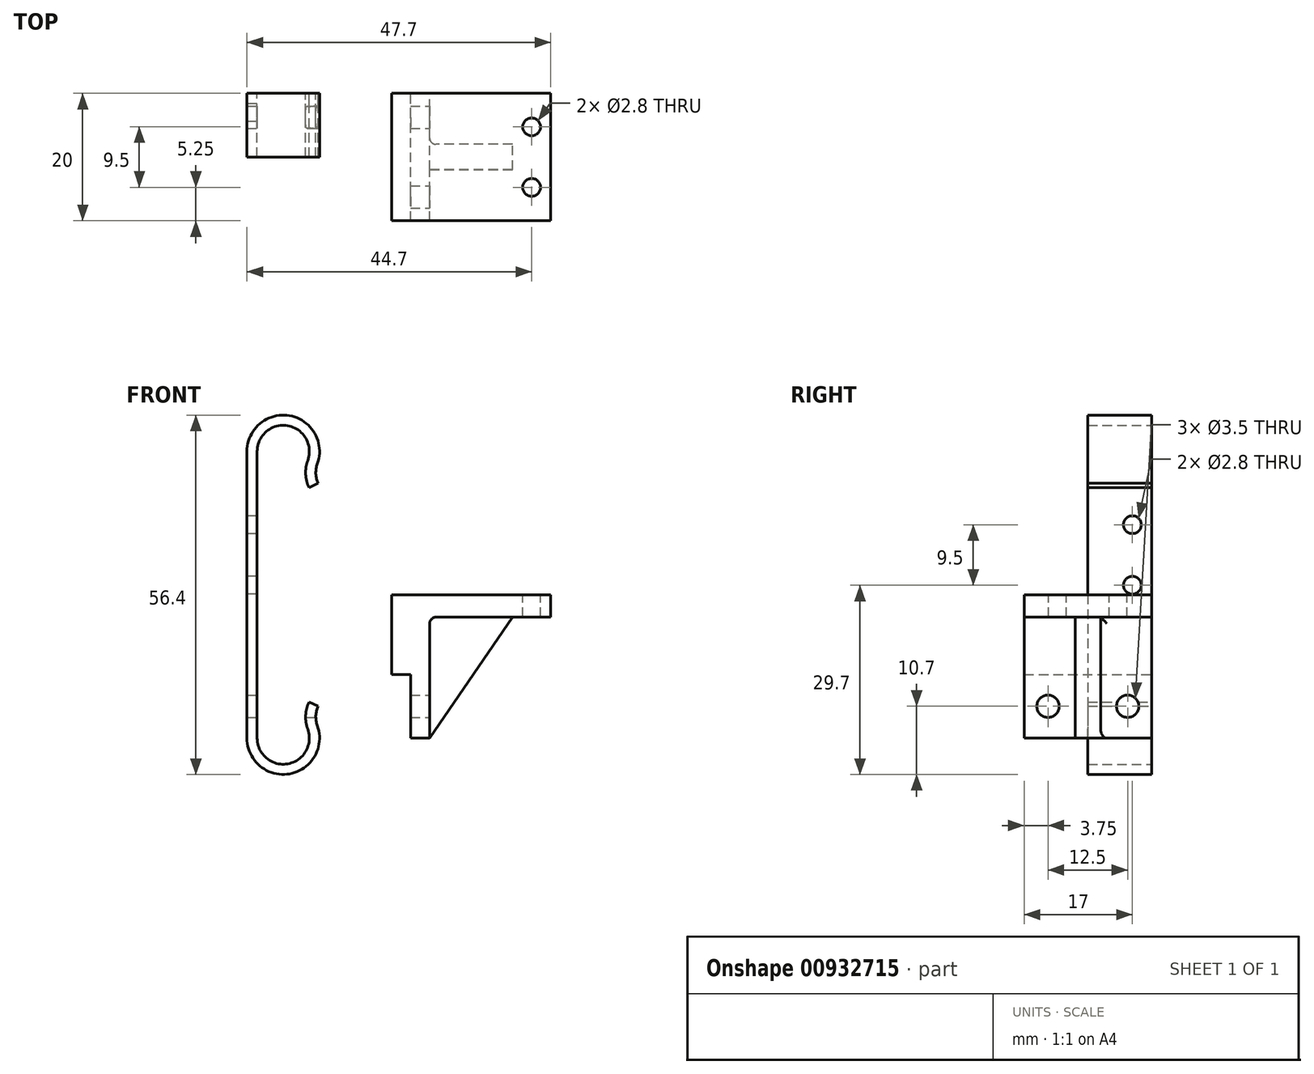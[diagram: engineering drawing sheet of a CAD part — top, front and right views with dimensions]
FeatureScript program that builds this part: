
annotation { "Feature Type Name" : "Feature", "Feature Type Description" : "" }
export const myFeature = defineFeature(function(context is Context, id is Id, definition is map)
    precondition{}
    {
        {
            var Q0;
            Q0=qCreatedBy(makeId("Front.planeOp"),FACE);
            var sketch = newSketch(context, id + "F0", { "sketchPlane" : qUnion([Q0])});
            skLineSegment(sketch, "E0", {"start": v(-25.7, 45) * mm, "end": v(-25.7, 0) * mm});
            skLineSegment(sketch, "E1", {"start": v(-24.1, 45) * mm, "end": v(-24.1, 0) * mm});
            skArc(sketch, "E2", {"start": v(-14.64, 43.05) * mm, "mid": v(-19.01, 50.61) * mm, "end": v(-25.7, 45) * mm});
            skArc(sketch, "E3", {"start": v(-16.15, 43.6) * mm, "mid": v(-19.29, 49.04) * mm, "end": v(-24.1, 45) * mm});
            skArc(sketch, "E4", {"start": v(-24.1, 0) * mm, "mid": v(-19.29, -4.04) * mm, "end": v(-16.15, 1.4) * mm});
            skArc(sketch, "E5", {"start": v(-25.7, 0) * mm, "mid": v(-19.01, -5.61) * mm, "end": v(-14.64, 1.95) * mm});
            skArc(sketch, "E6", {"start": v(-16.15, 43.6) * mm, "mid": v(-16.48, 41.44) * mm, "end": v(-15.96, 39.32) * mm});
            skArc(sketch, "E7", {"start": v(-15.96, 5.68) * mm, "mid": v(-16.48, 3.56) * mm, "end": v(-16.15, 1.4) * mm});
            skLineSegment(sketch, "E8", {"start": v(-20, 0) * mm, "end": v(-16.15, 1.4) * mm, "construction": true});
            skLineSegment(sketch, "E9", {"start": v(-20, 0) * mm, "end": v(-24.1, 0) * mm, "construction": true});
            skLineSegment(sketch, "E10", {"start": v(-10.88, 3.32) * mm, "end": v(-15.96, 5.68) * mm, "construction": true});
            skArc(sketch, "E11", {"start": v(-14.51, 5) * mm, "mid": v(-14.88, 3.5) * mm, "end": v(-14.64, 1.95) * mm});
            skArc(sketch, "E12", {"start": v(-14.64, 43.05) * mm, "mid": v(-14.88, 41.5) * mm, "end": v(-14.51, 40) * mm});
            skLineSegment(sketch, "E13", {"start": v(-14.51, 40) * mm, "end": v(-15.96, 39.32) * mm});
            skLineSegment(sketch, "E14", {"start": v(-20, 45) * mm, "end": v(-16.15, 43.6) * mm, "construction": true});
            skLineSegment(sketch, "E15", {"start": v(-15.96, 5.68) * mm, "end": v(-14.51, 5) * mm});
            skLineSegment(sketch, "E16", {"start": v(-20, 0) * mm, "end": v(0, 0) * mm, "construction": true});
            skSolve(sketch);
        }
        {
            var Q0;
            Q0=makeQuery(id+"F0.imprint","IMPRINT",FACE,{"disambiguationData":[TD([[makeQuery(id+"F0.imprint","IMPRINT",EDGE,{"derivedFrom":sQuery(id+"F0.wireOp",EDGE,"E0")}),1.0]])]});
            extrude(context, id + "F1", {"entities" : qUnion([Q0]), "depth" : 10 * mm, "offsetDistance" : 25 * mm});
        }
        {
            var Q0;
            Q0=makeQuery(id+"F1.opExtrude","SWEPT_FACE",FACE,{"disambiguationData":[OSD([sQuery(id+"F0.wireOp",EDGE,"E0")])]});
            var sketch = newSketch(context, id + "F2", { "sketchPlane" : qUnion([Q0])});
            skCircle(sketch, "E17", {"center": v(3, 33.5) * mm, "radius": 1.4 * mm});
            skCircle(sketch, "E18", {"center": v(3, 24) * mm, "radius": 1.4 * mm});
            skLineSegment(sketch, "E19", {"start": v(3, 33.5) * mm, "end": v(3, 24) * mm, "construction": true});
            skSolve(sketch);
        }
        {
            var Q0;
            Q0 = qSketchRegion(id + "F2", true);
            extrude(context, id + "F3", {"entities" : qUnion([Q0]), "operationType" : NewBodyOperationType.REMOVE, "endBound" : BoundingType.THROUGH_ALL, "oppositeDirection" : true, "depth" : 25 * mm, "offsetDistance" : 25 * mm});
        }
        {
            var Q0;
            Q0=qCreatedBy(makeId("Front.planeOp"),FACE);
            var sketch = newSketch(context, id + "F4", { "sketchPlane" : qUnion([Q0])});
            skLineSegment(sketch, "E20", {"start": v(0, 0) * mm, "end": v(0, 10) * mm});
            skLineSegment(sketch, "E21", {"start": v(0, 10) * mm, "end": v(-3, 10) * mm});
            skLineSegment(sketch, "E22", {"start": v(-3, 10) * mm, "end": v(-3, 22.5) * mm});
            skLineSegment(sketch, "E23", {"start": v(-3, 22.5) * mm, "end": v(22, 22.5) * mm});
            skLineSegment(sketch, "E24", {"start": v(22, 22.5) * mm, "end": v(22, 19) * mm});
            skLineSegment(sketch, "E25", {"start": v(22, 19) * mm, "end": v(3, 19) * mm});
            skLineSegment(sketch, "E26", {"start": v(3, 19) * mm, "end": v(3, 0) * mm});
            skLineSegment(sketch, "E27", {"start": v(3, 0) * mm, "end": v(0, 0) * mm});
            skSolve(sketch);
        }
        {
            var Q0;
            Q0=makeQuery(id+"F4.imprint","IMPRINT",FACE,{"disambiguationData":[TD([[makeQuery(id+"F4.imprint","IMPRINT",EDGE,{"derivedFrom":sQuery(id+"F4.wireOp",EDGE,"E20")}),-1.0]])]});
            extrude(context, id + "F5", {"entities" : qUnion([Q0]), "depth" : 20 * mm, "offsetDistance" : 25 * mm});
        }
        {
            var Q0;
            Q0=makeQuery(id+"F5.opExtrude","SWEPT_FACE",FACE,{"disambiguationData":[OSD([sQuery(id+"F4.wireOp",EDGE,"E23")])]});
            var sketch = newSketch(context, id + "F6", { "sketchPlane" : qUnion([Q0])});
            skCircle(sketch, "E28", {"center": v(19, -5.25) * mm, "radius": 1.4 * mm});
            skCircle(sketch, "E29", {"center": v(19, -14.75) * mm, "radius": 1.4 * mm});
            skLineSegment(sketch, "E30", {"start": v(19, -5.25) * mm, "end": v(19, -14.75) * mm, "construction": true});
            skLineSegment(sketch, "E31", {"start": v(19, -10) * mm, "end": v(22, -10) * mm, "construction": true});
            skSolve(sketch);
        }
        {
            var Q0;
            Q0 = qSketchRegion(id + "F6", true);
            extrude(context, id + "F7", {"entities" : qUnion([Q0]), "operationType" : NewBodyOperationType.REMOVE, "endBound" : BoundingType.THROUGH_ALL, "oppositeDirection" : true, "depth" : 25 * mm, "offsetDistance" : 25 * mm});
        }
        {
            var Q0;
            Q0=makeQuery(id+"F5.opExtrude","SWEPT_EDGE",EDGE,{"disambiguationData":[OSD([sQuery(id+"F4.wireOp",EDGE,"E24"),sQuery(id+"F4.wireOp",EDGE,"E25")])]});
            cPoint(context, id + "F8", {"entities" : qUnion([Q0]), "parameter" : 0.5});
        }
        {
            var Q0;
            Q0=makeQuery(id+"F5.opExtrude","CAP_FACE",FACE,{"disambiguationData":[OSD([sQuery(id+"F4.wireOp",EDGE,"E20"),sQuery(id+"F4.wireOp",EDGE,"E21"),sQuery(id+"F4.wireOp",EDGE,"E22"),sQuery(id+"F4.wireOp",EDGE,"E23"),sQuery(id+"F4.wireOp",EDGE,"E24"),sQuery(id+"F4.wireOp",EDGE,"E25"),sQuery(id+"F4.wireOp",EDGE,"E26"),sQuery(id+"F4.wireOp",EDGE,"E27")])],"isStart":false});
            var Q1;
            Q1 = qCreatedBy(id + "F8" ,VERTEX);
            cPlane(context, id + "F9", {"entities" : qUnion([Q0, Q1]), "cplaneType" : CPlaneType.PLANE_POINT, "offset" : 25 * mm, "width" : 150 * mm, "height" : 150 * mm});
        }
        {
            var Q0;
            Q0=qCreatedBy(id+"F9.planeOp",FACE);
            var sketch = newSketch(context, id + "F10", { "sketchPlane" : qUnion([Q0])});
            skLineSegment(sketch, "E32", {"start": v(3, 0) * mm, "end": v(16, 19) * mm});
            skLineSegment(sketch, "E33", {"start": v(16, 19) * mm, "end": v(3, 19) * mm});
            skLineSegment(sketch, "E34", {"start": v(3, 19) * mm, "end": v(3, 0) * mm});
            skSolve(sketch);
        }
        {
            var Q0;
            Q0=makeQuery(id+"F10.imprint","IMPRINT",FACE,{"disambiguationData":[TD([[makeQuery(id+"F10.imprint","IMPRINT",EDGE,{"derivedFrom":sQuery(id+"F10.wireOp",EDGE,"E32")}),1.0]])]});
            extrude(context, id + "F11", {"entities" : qUnion([Q0]), "operationType" : NewBodyOperationType.ADD, "endBound" : BoundingType.SYMMETRIC, "depth" : 4 * mm, "offsetDistance" : 25 * mm});
        }
        {
            var Q0;
            Q0=makeQuery(id+"F11.opExtrude","CAP_EDGE",EDGE,{"disambiguationData":[OSD([sQuery(id+"F10.wireOp",EDGE,"E33")])],"isStart":false});
            var Q1;
            Q1=makeQuery(id+"F11.opExtrude","CAP_EDGE",EDGE,{"disambiguationData":[OSD([sQuery(id+"F10.wireOp",EDGE,"E34")])],"isStart":false});
            var Q2;
            {var subQ0=sQuery(id+"F4.wireOp",EDGE,"E26");var subQ1=sQuery(id+"F4.wireOp",EDGE,"E25");Q2=makeQuery(id+"F11.boolean.opBoolean","SPLIT",EDGE,{"disambiguationData":[TD([makeQuery(id+"F11.opExtrude","CAP_FACE",FACE,{"disambiguationData":[OSD([sQuery(id+"F10.wireOp",EDGE,"E32"),sQuery(id+"F10.wireOp",EDGE,"E33"),sQuery(id+"F10.wireOp",EDGE,"E34")])],"isStart":false})])],"derivedFrom":makeQuery(id+"F5.opExtrude","SWEPT_EDGE",EDGE,{"disambiguationData":[OSD([subQ1,subQ0])]})});}
            var Q3;
            {var subQ0=sQuery(id+"F4.wireOp",EDGE,"E26");var subQ1=sQuery(id+"F4.wireOp",EDGE,"E25");Q3=makeQuery(id+"F11.boolean.opBoolean","SPLIT",EDGE,{"disambiguationData":[TD([makeQuery(id+"F11.opExtrude","CAP_FACE",FACE,{"disambiguationData":[OSD([sQuery(id+"F10.wireOp",EDGE,"E32"),sQuery(id+"F10.wireOp",EDGE,"E33"),sQuery(id+"F10.wireOp",EDGE,"E34")])],"isStart":true})])],"derivedFrom":makeQuery(id+"F5.opExtrude","SWEPT_EDGE",EDGE,{"disambiguationData":[OSD([subQ1,subQ0])]})});}
            var Q4;
            Q4=makeQuery(id+"F11.opExtrude","CAP_EDGE",EDGE,{"disambiguationData":[OSD([sQuery(id+"F10.wireOp",EDGE,"E33")])],"isStart":true});
            var Q5;
            Q5=makeQuery(id+"F11.opExtrude","CAP_EDGE",EDGE,{"disambiguationData":[OSD([sQuery(id+"F10.wireOp",EDGE,"E34")])],"isStart":true});
            var Q6;
            Q6=makeQuery(id+"F11.opExtrude","SWEPT_EDGE",EDGE,{"disambiguationData":[OSD([sQuery(id+"F10.wireOp",EDGE,"E32"),sQuery(id+"F10.wireOp",EDGE,"E33")])]});
            fillet(context, id + "F12", {"entities" : qUnion([Q0, Q1, Q2, Q3, Q4, Q5, Q6]), "radius" : 1 * mm, "tangentPropagation" : true, "allowEdgeOverflow" : false});
        }
        {
            var Q0;
            {var subQ0=sQuery(id+"F10.wireOp",EDGE,"E32");var subQ3=sQuery(id+"F4.wireOp",EDGE,"E26");Q0=makeQuery(id+"F11.boolean.opBoolean","SPLIT",FACE,{"disambiguationData":[TD([makeQuery(id+"F11.opExtrude","CAP_FACE",FACE,{"disambiguationData":[OSD([subQ0,sQuery(id+"F10.wireOp",EDGE,"E33"),sQuery(id+"F10.wireOp",EDGE,"E34")])],"isStart":false})])],"derivedFrom":makeQuery(id+"F5.opExtrude","SWEPT_FACE",FACE,{"disambiguationData":[OSD([subQ3])]})});}
            var sketch = newSketch(context, id + "F13", { "sketchPlane" : qUnion([Q0])});
            skCircle(sketch, "E35", {"center": v(-16.25, 5) * mm, "radius": 1.75 * mm});
            skCircle(sketch, "E36", {"center": v(-3.75, 5) * mm, "radius": 1.75 * mm});
            skLineSegment(sketch, "E37", {"start": v(-16.25, 5) * mm, "end": v(-3.75, 5) * mm, "construction": true});
            skLineSegment(sketch, "E38", {"start": v(-10, 5) * mm, "end": v(-10, 0) * mm, "construction": true});
            skSolve(sketch);
        }
        {
            var Q0;
            Q0 = qSketchRegion(id + "F13", true);
            extrude(context, id + "F14", {"entities" : qUnion([Q0]), "operationType" : NewBodyOperationType.REMOVE, "endBound" : BoundingType.THROUGH_ALL, "oppositeDirection" : true, "depth" : 25 * mm, "offsetDistance" : 25 * mm});
        }
    });
